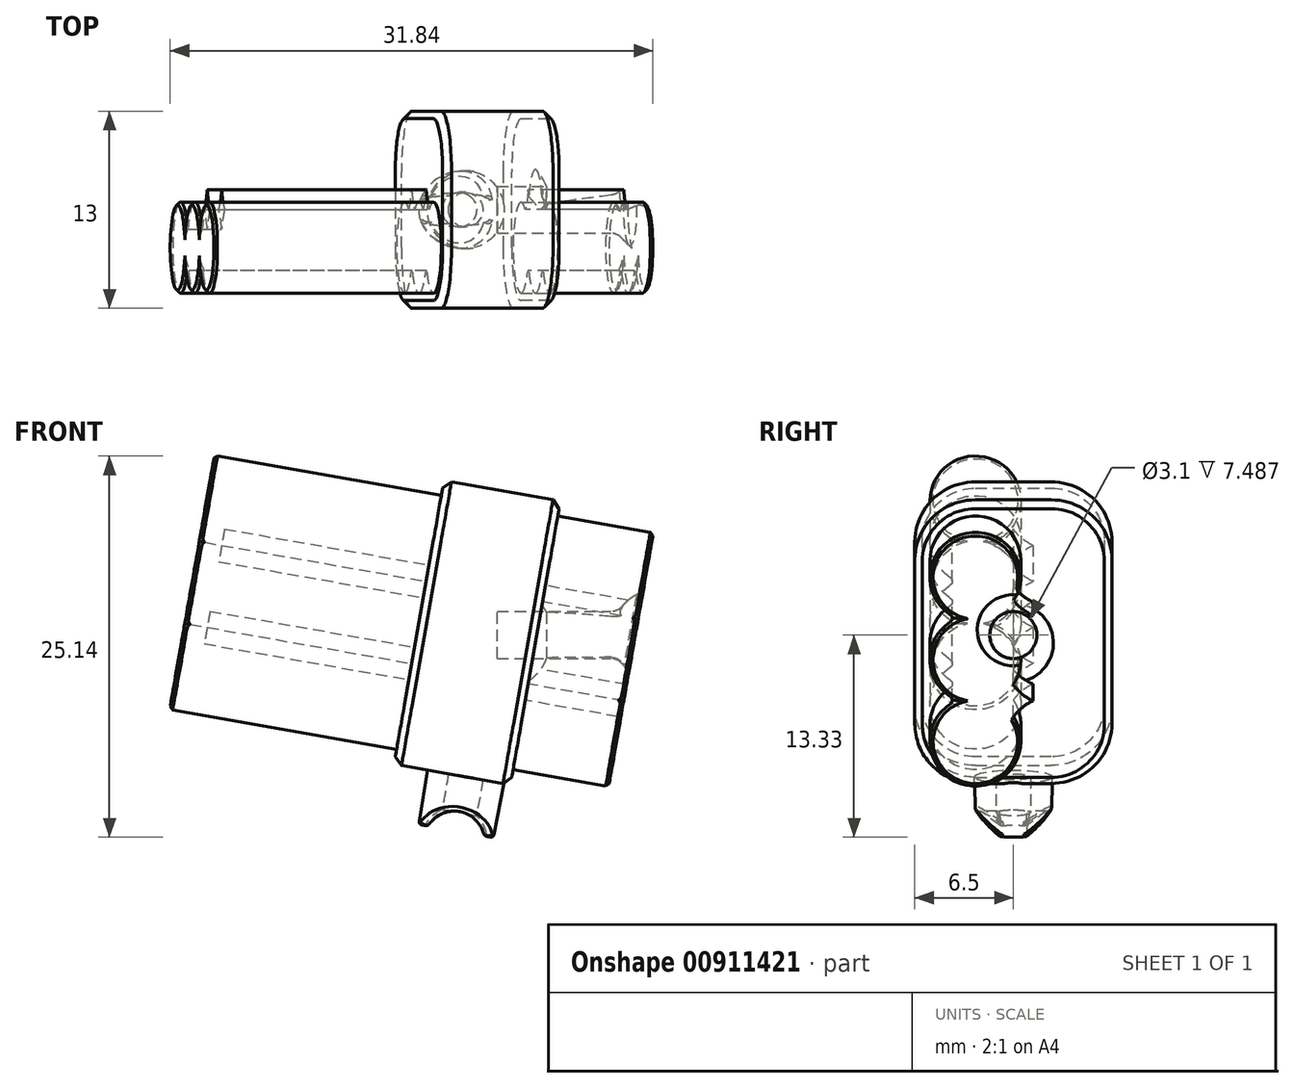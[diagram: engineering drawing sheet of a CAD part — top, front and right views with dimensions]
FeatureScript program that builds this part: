
annotation { "Feature Type Name" : "Feature", "Feature Type Description" : "" }
export const myFeature = defineFeature(function(context is Context, id is Id, definition is map)
    precondition{}
    {
        {
            var Q0;
            Q0=qCreatedBy(makeId("Front.planeOp"),FACE);
            var sketch = newSketch(context, id + "F0", { "sketchPlane" : qUnion([Q0])});
            skCircle(sketch, "E0", {"center": v(0, 0) * mm, "radius": 4 * mm});
            skCircle(sketch, "E1", {"center": v(11, 0) * mm, "radius": 3 * mm, "construction": true});
            skLineSegment(sketch, "E2.bottom", {"start": v(1.43, 1.55) * mm, "end": v(20.57, 1.55) * mm, "construction": true});
            skLineSegment(sketch, "E2.top", {"start": v(1.43, -1.55) * mm, "end": v(20.57, -1.55) * mm, "construction": true});
            skLineSegment(sketch, "E2.left", {"start": v(1.43, 1.55) * mm, "end": v(1.43, -1.55) * mm, "construction": true});
            skLineSegment(sketch, "E2.right", {"start": v(20.57, 1.55) * mm, "end": v(20.57, -1.55) * mm, "construction": true});
            skPoint(sketch, "E3", {"position": v(8.43, 1.55) * mm});
            skLineSegment(sketch, "E4", {"start": v(0, 0) * mm, "end": v(11, 0) * mm, "construction": true});
            skLineSegment(sketch, "E5", {"start": v(0, 0) * mm, "end": v(-2.38, -13.51) * mm, "construction": true});
            skCircle(sketch, "E6", {"center": v(-2.38, -13.51) * mm, "radius": 2 * mm, "construction": true});
            skLineSegment(sketch, "E7", {"start": v(-3.07, -11.63) * mm, "end": v(-2.2, -6.71) * mm, "construction": true});
            skLineSegment(sketch, "E8", {"start": v(-2.2, -6.71) * mm, "end": v(-0.23, -7.06) * mm, "construction": true});
            skLineSegment(sketch, "E9", {"start": v(-0.23, -7.06) * mm, "end": v(-1.1, -11.98) * mm, "construction": true});
            skPoint(sketch, "E10", {"position": v(-1.21, -6.88) * mm});
            skLineSegment(sketch, "E11", {"start": v(-3, -2.64) * mm, "end": v(-4.74, -12.49) * mm});
            skLineSegment(sketch, "E12", {"start": v(-4.74, -12.49) * mm, "end": v(0.18, -13.36) * mm});
            skLineSegment(sketch, "E13", {"start": v(0.18, -13.36) * mm, "end": v(1.92, -3.5) * mm});
            skLineSegment(sketch, "E14", {"start": v(1.92, -3.5) * mm, "end": v(-3, -2.64) * mm, "construction": true});
            skPoint(sketch, "E15", {"position": v(-0.54, -3.08) * mm});
            skSolve(sketch);
        }
        {
            var Q0;
            Q0=qCreatedBy(makeId("Front.planeOp"),FACE);
            var sketch = newSketch(context, id + "F1", { "sketchPlane" : qUnion([Q0])});
            skArc(sketch, "E16.0", {"start": v(0.7, 3.94) * mm, "mid": v(-3.49, 1.96) * mm, "end": v(-3, -2.64) * mm});
            skLineSegment(sketch, "E17.0", {"start": v(-3, -2.64) * mm, "end": v(-4.74, -12.49) * mm});
            skLineSegment(sketch, "E18.0", {"start": v(-4.74, -12.49) * mm, "end": v(-2.28, -12.92) * mm});
            skLineSegment(sketch, "E19.0", {"start": v(0, 0) * mm, "end": v(-2.28, -12.92) * mm});
            skLineSegment(sketch, "E20", {"start": v(0, 0) * mm, "end": v(0.7, 3.94) * mm});
            skPoint(sketch, "E21.orphan", {"position": v(0.18, -13.36) * mm});
            skPoint(sketch, "E22.orphan", {"position": v(-2.38, -13.51) * mm});
            skSolve(sketch);
        }
        {
            var Q0;
            Q0 = qSketchRegion(id + "F1", true);
            var Q1;
            Q1=sQuery(id+"F1.wireOp",EDGE,"E19.0");
            revolve(context, id + "F2", {"surfaceOperationType" : NewSurfaceOperationType.NEW, "entities" : qUnion([Q0]), "axis" : qUnion([Q1]), "revolveType" : RevolveType.FULL});
        }
        {
            var Q0;
            Q0=qCreatedBy(makeId("Front.planeOp"),FACE);
            var sketch = newSketch(context, id + "F3", { "sketchPlane" : qUnion([Q0])});
            skLineSegment(sketch, "E23.0", {"start": v(-2.2, -6.71) * mm, "end": v(-1.21, -6.88) * mm, "construction": true});
            skLineSegment(sketch, "E24.0", {"start": v(-3.07, -11.63) * mm, "end": v(-2.2, -6.71) * mm});
            skArc(sketch, "E25.0", {"start": v(-3.07, -11.63) * mm, "mid": v(-4.38, -13.69) * mm, "end": v(-2.73, -15.48) * mm, "construction": true});
            skLineSegment(sketch, "E26.0", {"start": v(-1.21, -6.88) * mm, "end": v(-2.38, -13.51) * mm});
            skLineSegment(sketch, "E27", {"start": v(-2.38, -13.51) * mm, "end": v(-2.73, -15.48) * mm});
            skPoint(sketch, "E28.orphan", {"position": v(-0.23, -7.06) * mm});
            skPoint(sketch, "E29.orphan", {"position": v(0, 0) * mm});
            skLineSegment(sketch, "E30.0", {"start": v(-3.2, -11.53) * mm, "end": v(-2.17, -5.7) * mm});
            skArc(sketch, "E31.0", {"start": v(-3.2, -11.53) * mm, "mid": v(-4.52, -13.75) * mm, "end": v(-2.76, -15.63) * mm});
            skLineSegment(sketch, "E32.0", {"start": v(-2.17, -5.7) * mm, "end": v(-1.04, -5.9) * mm});
            skLineSegment(sketch, "E33", {"start": v(-2.76, -15.63) * mm, "end": v(-2.73, -15.48) * mm});
            skLineSegment(sketch, "E34", {"start": v(-1.04, -5.9) * mm, "end": v(-1.21, -6.88) * mm});
            skSolve(sketch);
        }
        {
            var Q0;
            Q0 = qSketchRegion(id + "F3", true);
            var Q1;
            Q1=sQuery(id+"F3.wireOp",EDGE,"E27");
            revolve(context, id + "F4", {"operationType" : NewBodyOperationType.REMOVE, "surfaceOperationType" : NewSurfaceOperationType.NEW, "entities" : qUnion([Q0]), "axis" : qUnion([Q1]), "revolveType" : RevolveType.FULL, "oppositeDirection" : true});
        }
        {
            var Q0;
            Q0=qCreatedBy(makeId("Front.planeOp"),FACE);
            var sketch = newSketch(context, id + "F5", { "sketchPlane" : qUnion([Q0])});
            skCircle(sketch, "E35.0", {"center": v(-2.38, -13.51) * mm, "radius": 2 * mm, "construction": true});
            skLineSegment(sketch, "E36.0", {"start": v(0, 0) * mm, "end": v(-2.38, -13.51) * mm, "construction": true});
            skLineSegment(sketch, "E37", {"start": v(-2.38, -13.51) * mm, "end": v(-2.4, -13.61) * mm, "construction": true});
            skCircle(sketch, "E38", {"center": v(-2.4, -13.61) * mm, "radius": 2 * mm});
            skSolve(sketch);
        }
        {
            var Q0;
            Q0=qCreatedBy(makeId("Front.planeOp"),FACE);
            var sketch = newSketch(context, id + "F6", { "sketchPlane" : qUnion([Q0])});
            skLineSegment(sketch, "E39", {"start": v(1.92, -3.5) * mm, "end": v(0.18, -13.36) * mm, "construction": true});
            skLineSegment(sketch, "E40", {"start": v(-4.74, -12.49) * mm, "end": v(-3, -2.64) * mm});
            skLineSegment(sketch, "E41.0", {"start": v(0, 0) * mm, "end": v(-2.38, -13.51) * mm, "construction": true});
            skLineSegment(sketch, "E42", {"start": v(-4.74, -12.49) * mm, "end": v(-3, -1.47) * mm});
            skLineSegment(sketch, "E43", {"start": v(-3, -1.47) * mm, "end": v(-3, -2.64) * mm});
            skSolve(sketch);
        }
        {
            var Q0;
            Q0 = qSketchRegion(id + "F6", true);
            var Q1;
            Q1=sQuery(id+"F6.wireOp",EDGE,"E41.0");
            revolve(context, id + "F7", {"operationType" : NewBodyOperationType.ADD, "surfaceOperationType" : NewSurfaceOperationType.NEW, "entities" : qUnion([Q0]), "axis" : qUnion([Q1]), "revolveType" : RevolveType.FULL});
        }
        {
            var Q0;
            Q0 = qSketchRegion(id + "F5", true);
            extrude(context, id + "F8", {"entities" : qUnion([Q0]), "operationType" : NewBodyOperationType.REMOVE, "endBound" : BoundingType.SYMMETRIC, "oppositeDirection" : true, "depth" : 7.52 * mm, "offsetDistance" : 25 * mm});
        }
        {
            var Q0;
            Q0=qCreatedBy(makeId("Front.planeOp"),FACE);
            cPlane(context, id + "F9", {"entities" : qUnion([Q0]), "cplaneType" : CPlaneType.OFFSET, "offset" : 2.5 * mm, "width" : 150 * mm, "height" : 150 * mm});
        }
        {
            var Q0;
            Q0=qCreatedBy(makeId("Front.planeOp"),FACE);
            var sketch = newSketch(context, id + "F10", { "sketchPlane" : qUnion([Q0])});
            skLineSegment(sketch, "E44", {"start": v(0, 0) * mm, "end": v(4.68, 26.57) * mm});
            skLineSegment(sketch, "E45", {"start": v(4.68, 26.57) * mm, "end": v(4.68, 0) * mm, "construction": true});
            skLineSegment(sketch, "E46", {"start": v(4.68, 0) * mm, "end": v(0, 0) * mm, "construction": true});
            skSolve(sketch);
        }
        {
            var Q0;
            Q0=qCreatedBy(id+"F9.planeOp",FACE);
            var Q1;
            Q1=sQuery(id+"F10.wireOp",EDGE,"E44");
            cPlane(context, id + "F11", {"entities" : qUnion([Q0, Q1]), "cplaneType" : CPlaneType.LINE_ANGLE, "offset" : 25 * mm, "angle" : 90 * degree, "width" : 150 * mm, "height" : 150 * mm});
        }
        {
            var Q0;
            Q0=qCreatedBy(id+"F9.planeOp",FACE);
            var sketch = newSketch(context, id + "F12", { "sketchPlane" : qUnion([Q0])});
            skLineSegment(sketch, "E47.0", {"start": v(0, 0) * mm, "end": v(4.68, 26.57) * mm});
            skArc(sketch, "E48", {"start": v(2.12, -3.4) * mm, "mid": v(0.7, 3.94) * mm, "end": v(-3.15, -2.46) * mm});
            skLineSegment(sketch, "E49", {"start": v(2.12, -3.4) * mm, "end": v(0.18, -13.36) * mm});
            skLineSegment(sketch, "E50", {"start": v(-4.74, -12.49) * mm, "end": v(-3.15, -2.46) * mm});
            skSolve(sketch);
        }
        {
            var Q0;
            Q0=qCreatedBy(id+"F11.planeOp",FACE);
            var sketch = newSketch(context, id + "F13", { "sketchPlane" : qUnion([Q0])});
            skPoint(sketch, "E51.0", {"position": v(2.5, 0) * mm});
            skLineSegment(sketch, "E52.0", {"start": v(2.5, 0) * mm, "end": v(2.5, 26.98) * mm, "construction": true});
            skLineSegment(sketch, "E53", {"start": v(2.5, 0) * mm, "end": v(15.85, 0) * mm, "construction": true});
            skCircle(sketch, "E54", {"center": v(2.5, 0) * mm, "radius": 3 * mm});
            skCircle(sketch, "E55", {"center": v(2.5, 5.5) * mm, "radius": 3 * mm});
            skCircle(sketch, "E56.MirrorC", {"center": v(2.5, -5.5) * mm, "radius": 3 * mm});
            skSolve(sketch);
        }
        {
            var Q0;
            Q0 = qSketchRegion(id + "F13", true);
            extrude(context, id + "F14", {"entities" : qUnion([Q0]), "operationType" : NewBodyOperationType.ADD, "depth" : 20 * mm, "offsetDistance" : 25 * mm, "hasSecondDirection" : true, "secondDirectionOppositeDirection" : true, "secondDirectionDepth" : 9.4 * mm});
        }
        {
            var Q0;
            Q0=qCreatedBy(id+"F11.planeOp",FACE);
            var sketch = newSketch(context, id + "F15", { "sketchPlane" : qUnion([Q0])});
            skArc(sketch, "E57.0.0", {"start": v(3.7, 2.75) * mm, "mid": v(2.5, 8.5) * mm, "end": v(1.3, 2.75) * mm, "construction": true});
            skArc(sketch, "E57.0.1", {"start": v(1.3, 2.75) * mm, "mid": v(-0.5, 0) * mm, "end": v(1.3, -2.75) * mm});
            skArc(sketch, "E57.0.2", {"start": v(1.3, -2.75) * mm, "mid": v(2.5, -8.5) * mm, "end": v(3.7, -2.75) * mm});
            skArc(sketch, "E57.0.3", {"start": v(3.7, -2.75) * mm, "mid": v(5.5, 0) * mm, "end": v(3.7, 2.75) * mm});
            skLineSegment(sketch, "E58.bottom", {"start": v(2.5, -9.5) * mm, "end": v(-2.5, -9.5) * mm});
            skLineSegment(sketch, "E58.top", {"start": v(2.5, 9.5) * mm, "end": v(-2.5, 9.5) * mm});
            skLineSegment(sketch, "E58.left", {"start": v(6.5, -5.5) * mm, "end": v(6.5, 5.5) * mm});
            skLineSegment(sketch, "E58.right", {"start": v(-6.5, -5.5) * mm, "end": v(-6.5, 5.5) * mm});
            skPoint(sketch, "E58.middle", {"position": v(0, 0) * mm});
            skPoint(sketch, "E59.visualSharp", {"position": v(6.5, 9.5) * mm});
            skArc(sketch, "E59.filletArc", {"start": v(6.5, 5.5) * mm, "mid": v(5.33, 8.33) * mm, "end": v(2.5, 9.5) * mm});
            skPoint(sketch, "E60.visualSharp", {"position": v(6.5, -9.5) * mm});
            skArc(sketch, "E60.filletArc", {"start": v(2.5, -9.5) * mm, "mid": v(5.33, -8.33) * mm, "end": v(6.5, -5.5) * mm});
            skPoint(sketch, "E61.visualSharp", {"position": v(-6.5, 9.5) * mm});
            skArc(sketch, "E61.filletArc", {"start": v(-2.5, 9.5) * mm, "mid": v(-5.33, 8.33) * mm, "end": v(-6.5, 5.5) * mm});
            skPoint(sketch, "E62.visualSharp", {"position": v(-6.5, -9.5) * mm});
            skArc(sketch, "E62.filletArc", {"start": v(-6.5, -5.5) * mm, "mid": v(-5.33, -8.33) * mm, "end": v(-2.5, -9.5) * mm});
            skSolve(sketch);
        }
        {
            var Q0;
            Q0 = qSketchRegion(id + "F15", true);
            extrude(context, id + "F16", {"entities" : qUnion([Q0]), "operationType" : NewBodyOperationType.ADD, "depth" : 4.8 * mm, "offsetDistance" : 25 * mm, "hasSecondDirection" : true, "secondDirectionOppositeDirection" : true, "secondDirectionDepth" : 3 * mm});
        }
        {
            var Q0;
            {var subQ0=sQuery(id+"F15.wireOp",EDGE,"E58.right");var subQ1=sQuery(id+"F15.wireOp",EDGE,"E58.left");var subQ2=sQuery(id+"F15.wireOp",EDGE,"E58.bottom");var subQ3=sQuery(id+"F13.wireOp",EDGE,"E56.MirrorC");var subQ4=sQuery(id+"F13.wireOp",EDGE,"E55");var subQ5=sQuery(id+"F15.wireOp",EDGE,"E62.filletArc");var subQ6=sQuery(id+"F13.wireOp",EDGE,"E54");var subQ7=makeQuery(id+"F13.imprint","IMPRINT",EDGE,{"disambiguationData":[TD([[makeQuery(id+"F13.imprint","INTERSECT",VERTEX,{"disambiguationData":[OD(1.0)],"derivedFrom":[subQ6,subQ4]}),1.0]])],"derivedFrom":subQ6});var subQ8=sQuery(id+"F15.wireOp",EDGE,"E58.top");var subQ9=sQuery(id+"F15.wireOp",EDGE,"E61.filletArc");var subQ10=sQuery(id+"F15.wireOp",EDGE,"E59.filletArc");var subQ11=sQuery(id+"F15.wireOp",EDGE,"E60.filletArc");Q0=makeQuery(id+"F16.boolean.opBoolean","SPLIT",FACE,{"disambiguationData":[TD([makeQuery(id+"F14.opExtrude","SWEPT_FACE",FACE,{"disambiguationData":[OSD([subQ6]),TDD([subQ7])]}),makeQuery(id+"F14.opExtrude","SWEPT_FACE",FACE,{"disambiguationData":[OSD([subQ4])]}),makeQuery(id+"F14.opExtrude","SWEPT_FACE",FACE,{"disambiguationData":[OSD([subQ3])]}),makeQuery(id+"FyxM6r6C1p8SssR_1.1.F14.opExtrude","SWEPT_FACE",FACE,{"disambiguationData":[OSD([subQ6]),TDD([subQ7])]}),makeQuery(id+"FyxM6r6C1p8SssR_1.1.F14.opExtrude","SWEPT_FACE",FACE,{"disambiguationData":[OSD([subQ4])]}),makeQuery(id+"FyxM6r6C1p8SssR_1.1.F14.opExtrude","SWEPT_FACE",FACE,{"disambiguationData":[OSD([subQ3])]}),makeQuery(id+"F16.opExtrude","SWEPT_FACE",FACE,{"disambiguationData":[OSD([subQ2])]}),makeQuery(id+"F16.opExtrude","SWEPT_FACE",FACE,{"disambiguationData":[OSD([subQ8])]}),makeQuery(id+"F16.opExtrude","SWEPT_FACE",FACE,{"disambiguationData":[OSD([subQ1])]}),makeQuery(id+"F16.opExtrude","SWEPT_FACE",FACE,{"disambiguationData":[OSD([subQ0])]}),makeQuery(id+"F16.opExtrude","SWEPT_FACE",FACE,{"disambiguationData":[OSD([subQ10])]}),makeQuery(id+"F16.opExtrude","SWEPT_FACE",FACE,{"disambiguationData":[OSD([subQ11])]}),makeQuery(id+"F16.opExtrude","SWEPT_FACE",FACE,{"disambiguationData":[OSD([subQ9])]}),makeQuery(id+"F16.opExtrude","SWEPT_FACE",FACE,{"disambiguationData":[OSD([subQ5])]})])],"derivedFrom":makeQuery(id+"F16.opExtrude","CAP_FACE",FACE,{"disambiguationData":[OSD([subQ2,subQ8,subQ1,subQ0,subQ10,subQ11,subQ9,subQ5])],"isStart":false})});}
            var sketch = newSketch(context, id + "F17", { "sketchPlane" : qUnion([Q0])});
            skArc(sketch, "E63.0", {"start": v(0, 3.84) * mm, "mid": v(-0.57, 3.2) * mm, "end": v(-1.3, 2.75) * mm});
            skArc(sketch, "E64.0", {"start": v(0, 3.84) * mm, "mid": v(0.57, 3.2) * mm, "end": v(1.3, 2.75) * mm});
            skArc(sketch, "E65.0", {"start": v(-1.3, 2.75) * mm, "mid": v(-0.57, 2.3) * mm, "end": v(0, 1.66) * mm});
            skArc(sketch, "E66.0", {"start": v(1.3, 2.75) * mm, "mid": v(0.57, 2.3) * mm, "end": v(0, 1.66) * mm});
            skArc(sketch, "E67.0", {"start": v(0, -1.66) * mm, "mid": v(-0.57, -2.3) * mm, "end": v(-1.3, -2.75) * mm});
            skArc(sketch, "E68.0", {"start": v(0, -1.66) * mm, "mid": v(0.57, -2.3) * mm, "end": v(1.3, -2.75) * mm});
            skArc(sketch, "E69.0", {"start": v(0, -3.84) * mm, "mid": v(0.57, -3.2) * mm, "end": v(1.3, -2.75) * mm});
            skArc(sketch, "E70.0", {"start": v(0, -3.84) * mm, "mid": v(-0.57, -3.2) * mm, "end": v(-1.3, -2.75) * mm});
            skSolve(sketch);
        }
        {
            var Q0;
            Q0 = qSketchRegion(id + "F17", true);
            var Q1;
            {var subQ0=sQuery(id+"F13.wireOp",EDGE,"E56.MirrorC");var subQ1=sQuery(id+"F13.wireOp",EDGE,"E55");var subQ2=sQuery(id+"F13.wireOp",EDGE,"E54");Q1=makeQuery(id+"FyxM6r6C1p8SssR_1.1.F14.boolean.opBoolean","MERGE",FACE,{"derivedFrom":[makeQuery(id+"F14.opExtrude","CAP_FACE",FACE,{"disambiguationData":[OSD([subQ2,subQ1,subQ0])],"isStart":false}),makeQuery(id+"FyxM6r6C1p8SssR_1.1.F14.opExtrude","CAP_FACE",FACE,{"disambiguationData":[OSD([subQ2,subQ1,subQ0])],"isStart":false})]});}
            var Q2;
            {var subQ0=sQuery(id+"F13.wireOp",EDGE,"E55");Q2=makeQuery(id+"FyxM6r6C1p8SssR_1.1.F14.boolean.opBoolean","INTERSECT",VERTEX,{"disambiguationData":[OD(2.0)],"derivedFrom":[makeQuery(id+"F14.opExtrude","SWEPT_FACE",FACE,{"disambiguationData":[OSD([subQ0])]}),makeQuery(id+"FyxM6r6C1p8SssR_1.1.F14.opExtrude","SWEPT_FACE",FACE,{"disambiguationData":[OSD([subQ0])]})]});}
            extrude(context, id + "F18", {"entities" : qUnion([Q0]), "operationType" : NewBodyOperationType.ADD, "endBound" : BoundingType.UP_TO_SURFACE, "depth" : 25 * mm, "endBoundEntityFace" : qUnion([Q1]), "endBoundEntityVertex" : qUnion([Q2]), "hasOffset" : true, "offsetDistance" : 1.5 * mm});
        }
        {
            var Q0;
            {var subQ0=sQuery(id+"F15.wireOp",EDGE,"E58.right");var subQ1=sQuery(id+"F15.wireOp",EDGE,"E58.left");var subQ2=sQuery(id+"F15.wireOp",EDGE,"E58.bottom");var subQ3=sQuery(id+"F13.wireOp",EDGE,"E56.MirrorC");var subQ4=sQuery(id+"F13.wireOp",EDGE,"E55");var subQ5=sQuery(id+"F15.wireOp",EDGE,"E62.filletArc");var subQ6=sQuery(id+"F13.wireOp",EDGE,"E54");var subQ7=makeQuery(id+"F13.imprint","IMPRINT",EDGE,{"disambiguationData":[TD([[makeQuery(id+"F13.imprint","INTERSECT",VERTEX,{"disambiguationData":[OD(1.0)],"derivedFrom":[subQ6,subQ4]}),1.0]])],"derivedFrom":subQ6});var subQ8=sQuery(id+"F15.wireOp",EDGE,"E58.top");var subQ9=sQuery(id+"F15.wireOp",EDGE,"E61.filletArc");var subQ10=sQuery(id+"F15.wireOp",EDGE,"E59.filletArc");var subQ11=sQuery(id+"F15.wireOp",EDGE,"E60.filletArc");Q0=makeQuery(id+"F16.boolean.opBoolean","SPLIT",FACE,{"disambiguationData":[TD([makeQuery(id+"F14.opExtrude","SWEPT_FACE",FACE,{"disambiguationData":[OSD([subQ6]),TDD([subQ7])]}),makeQuery(id+"F14.opExtrude","SWEPT_FACE",FACE,{"disambiguationData":[OSD([subQ4])]}),makeQuery(id+"F14.opExtrude","SWEPT_FACE",FACE,{"disambiguationData":[OSD([subQ3])]}),makeQuery(id+"FyxM6r6C1p8SssR_1.1.F14.opExtrude","SWEPT_FACE",FACE,{"disambiguationData":[OSD([subQ6]),TDD([subQ7])]}),makeQuery(id+"FyxM6r6C1p8SssR_1.1.F14.opExtrude","SWEPT_FACE",FACE,{"disambiguationData":[OSD([subQ4])]}),makeQuery(id+"FyxM6r6C1p8SssR_1.1.F14.opExtrude","SWEPT_FACE",FACE,{"disambiguationData":[OSD([subQ3])]}),makeQuery(id+"F16.opExtrude","SWEPT_FACE",FACE,{"disambiguationData":[OSD([subQ2])]}),makeQuery(id+"F16.opExtrude","SWEPT_FACE",FACE,{"disambiguationData":[OSD([subQ8])]}),makeQuery(id+"F16.opExtrude","SWEPT_FACE",FACE,{"disambiguationData":[OSD([subQ1])]}),makeQuery(id+"F16.opExtrude","SWEPT_FACE",FACE,{"disambiguationData":[OSD([subQ0])]}),makeQuery(id+"F16.opExtrude","SWEPT_FACE",FACE,{"disambiguationData":[OSD([subQ10])]}),makeQuery(id+"F16.opExtrude","SWEPT_FACE",FACE,{"disambiguationData":[OSD([subQ11])]}),makeQuery(id+"F16.opExtrude","SWEPT_FACE",FACE,{"disambiguationData":[OSD([subQ9])]}),makeQuery(id+"F16.opExtrude","SWEPT_FACE",FACE,{"disambiguationData":[OSD([subQ5])]})])],"derivedFrom":makeQuery(id+"F16.opExtrude","CAP_FACE",FACE,{"disambiguationData":[OSD([subQ2,subQ8,subQ1,subQ0,subQ10,subQ11,subQ9,subQ5])],"isStart":true})});}
            var sketch = newSketch(context, id + "F19", { "sketchPlane" : qUnion([Q0])});
            skArc(sketch, "E71.0", {"start": v(0, 3.84) * mm, "mid": v(0.57, 3.2) * mm, "end": v(1.3, 2.75) * mm});
            skArc(sketch, "E71.1", {"start": v(0, 3.84) * mm, "mid": v(-0.57, 3.2) * mm, "end": v(-1.3, 2.75) * mm});
            skArc(sketch, "E71.2", {"start": v(1.3, 2.75) * mm, "mid": v(0.57, 2.3) * mm, "end": v(0, 1.66) * mm});
            skArc(sketch, "E71.3", {"start": v(-1.3, 2.75) * mm, "mid": v(-0.57, 2.3) * mm, "end": v(0, 1.66) * mm});
            skArc(sketch, "E71.4", {"start": v(0, -1.66) * mm, "mid": v(0.57, -2.3) * mm, "end": v(1.3, -2.75) * mm});
            skArc(sketch, "E71.5", {"start": v(0, -1.66) * mm, "mid": v(-0.57, -2.3) * mm, "end": v(-1.3, -2.75) * mm});
            skArc(sketch, "E71.6", {"start": v(0, -3.84) * mm, "mid": v(-0.57, -3.2) * mm, "end": v(-1.3, -2.75) * mm});
            skArc(sketch, "E71.7", {"start": v(0, -3.84) * mm, "mid": v(0.57, -3.2) * mm, "end": v(1.3, -2.75) * mm});
            skSolve(sketch);
        }
        {
            var Q0;
            Q0 = qSketchRegion(id + "F19", true);
            var Q1;
            {var subQ0=sQuery(id+"F13.wireOp",EDGE,"E56.MirrorC");var subQ1=sQuery(id+"F13.wireOp",EDGE,"E55");var subQ2=sQuery(id+"F13.wireOp",EDGE,"E54");Q1=makeQuery(id+"FyxM6r6C1p8SssR_1.1.F14.boolean.opBoolean","MERGE",FACE,{"derivedFrom":[makeQuery(id+"F14.opExtrude","CAP_FACE",FACE,{"disambiguationData":[OSD([subQ2,subQ1,subQ0])],"isStart":true}),makeQuery(id+"FyxM6r6C1p8SssR_1.1.F14.opExtrude","CAP_FACE",FACE,{"disambiguationData":[OSD([subQ2,subQ1,subQ0])],"isStart":true})]});}
            extrude(context, id + "F20", {"entities" : qUnion([Q0]), "operationType" : NewBodyOperationType.ADD, "endBound" : BoundingType.UP_TO_SURFACE, "depth" : 25 * mm, "endBoundEntityFace" : qUnion([Q1]), "offsetDistance" : 1.5 * mm});
        }
        {
            var Q0;
            Q0=makeQuery(id+"F16.opExtrude","CAP_EDGE",EDGE,{"disambiguationData":[OSD([sQuery(id+"F15.wireOp",EDGE,"E58.left")])],"isStart":false});
            var Q1;
            Q1=makeQuery(id+"F16.opExtrude","CAP_EDGE",EDGE,{"disambiguationData":[OSD([sQuery(id+"F15.wireOp",EDGE,"E59.filletArc")])],"isStart":true});
            chamfer(context, id + "F21", {"entities" : qUnion([Q0, Q1]), "width" : 0.5 * mm, "tangentPropagation" : true});
        }
        {
            var Q0;
            Q0=qCreatedBy(makeId("Front.planeOp"),FACE);
            var sketch = newSketch(context, id + "F22", { "sketchPlane" : qUnion([Q0])});
            skLineSegment(sketch, "E72.0", {"start": v(8.15, -1.55) * mm, "end": v(8.27, -1.55) * mm});
            skLineSegment(sketch, "E73.0", {"start": v(1.43, 0) * mm, "end": v(1.43, -1.55) * mm});
            skPoint(sketch, "E74.0", {"position": v(20.57, 0) * mm});
            skLineSegment(sketch, "E75.0", {"start": v(20.57, 1.55) * mm, "end": v(20.57, -1.55) * mm});
            skLineSegment(sketch, "E76.0", {"start": v(0.43, 1.55) * mm, "end": v(8.43, 1.55) * mm});
            skLineSegment(sketch, "E77.0", {"start": v(0.43, 1.55) * mm, "end": v(0.43, 0) * mm});
            skLineSegment(sketch, "E78", {"start": v(20.57, 1.55) * mm, "end": v(20.57, 0) * mm});
            skLineSegment(sketch, "E79", {"start": v(0.43, 0) * mm, "end": v(20.57, 0) * mm});
            skArc(sketch, "E80.trimOffspring", {"start": v(13.57, 1.55) * mm, "mid": v(11, 3) * mm, "end": v(8.43, 1.55) * mm});
            skLineSegment(sketch, "E81.trimOffspring", {"start": v(13.57, 1.55) * mm, "end": v(20.57, 1.55) * mm});
            skPoint(sketch, "E82.orphan", {"position": v(1.43, 1.55) * mm});
            skPoint(sketch, "E83.orphan", {"position": v(20.57, -1.55) * mm});
            skPoint(sketch, "E84.orphan", {"position": v(1.43, -1.55) * mm});
            skLineSegment(sketch, "E85.trimOffspring", {"start": v(11.73, -1.55) * mm, "end": v(11.85, -1.55) * mm});
            skPoint(sketch, "E86.0.end.orphan", {"position": v(20.57, 1.55) * mm});
            skSolve(sketch);
        }
        {
            var Q0;
            Q0=makeQuery(id+"F22.imprint","IMPRINT",FACE,{"disambiguationData":[TD([[makeQuery(id+"F22.imprint","IMPRINT",EDGE,{"derivedFrom":sQuery(id+"F22.wireOp",EDGE,"E76.0")}),-1.0]])]});
            var Q1;
            Q1=sQuery(id+"F22.wireOp",EDGE,"E79");
            revolve(context, id + "F23", {"operationType" : NewBodyOperationType.REMOVE, "surfaceOperationType" : NewSurfaceOperationType.NEW, "entities" : qUnion([Q0]), "axis" : qUnion([Q1]), "revolveType" : RevolveType.FULL, "oppositeDirection" : true});
        }
        {
            var Q0;
            {var subQ1=sQuery(id+"F13.wireOp",EDGE,"E55");var subQ2=sQuery(id+"F13.wireOp",EDGE,"E54");Q0=makeQuery(id+"FyxM6r6C1p8SssR_1.1.F14.boolean.opBoolean","SPLIT",EDGE,{"disambiguationData":[TD([makeQuery(id+"F14.opExtrude","SWEPT_FACE",FACE,{"disambiguationData":[OSD([subQ2]),TDD([makeQuery(id+"F13.imprint","IMPRINT",EDGE,{"disambiguationData":[TD([[makeQuery(id+"F13.imprint","INTERSECT",VERTEX,{"disambiguationData":[OD(1.0)],"derivedFrom":[subQ2,subQ1]}),1.0]])],"derivedFrom":subQ2})])]})])],"derivedFrom":makeQuery(id+"F14.opExtrude","CAP_EDGE",EDGE,{"disambiguationData":[OSD([subQ1])],"isStart":false})});}
            var Q1;
            {var subQ0=sQuery(id+"F13.wireOp",EDGE,"E54");Q1=makeQuery(id+"F14.opExtrude","CAP_EDGE",EDGE,{"disambiguationData":[OSD([subQ0]),TDD([makeQuery(id+"F13.imprint","IMPRINT",EDGE,{"disambiguationData":[TD([[makeQuery(id+"F13.imprint","INTERSECT",VERTEX,{"disambiguationData":[OD(1.0)],"derivedFrom":[subQ0,sQuery(id+"F13.wireOp",EDGE,"E55")]}),1.0]])],"derivedFrom":subQ0})])],"isStart":false});}
            var Q2;
            {var subQ0=sQuery(id+"F13.wireOp",EDGE,"E56.MirrorC");var subQ1=sQuery(id+"F13.wireOp",EDGE,"E55");var subQ2=sQuery(id+"F13.wireOp",EDGE,"E54");Q2=makeQuery(id+"FyxM6r6C1p8SssR_1.1.F14.boolean.opBoolean","SPLIT",EDGE,{"disambiguationData":[TD([makeQuery(id+"F14.opExtrude","SWEPT_FACE",FACE,{"disambiguationData":[OSD([subQ2]),TDD([makeQuery(id+"F13.imprint","IMPRINT",EDGE,{"disambiguationData":[TD([[makeQuery(id+"F13.imprint","INTERSECT",VERTEX,{"disambiguationData":[OD(1.0)],"derivedFrom":[subQ2,subQ1]}),1.0]])],"derivedFrom":subQ2})])]})])],"derivedFrom":makeQuery(id+"F14.opExtrude","CAP_EDGE",EDGE,{"disambiguationData":[OSD([subQ0])],"isStart":false})});}
            var Q3;
            {var subQ0=sQuery(id+"F13.wireOp",EDGE,"E56.MirrorC");var subQ1=sQuery(id+"F13.wireOp",EDGE,"E55");var subQ2=sQuery(id+"F13.wireOp",EDGE,"E54");Q3=makeQuery(id+"FyxM6r6C1p8SssR_1.1.F14.boolean.opBoolean","SPLIT",EDGE,{"disambiguationData":[TD([makeQuery(id+"FyxM6r6C1p8SssR_1.1.F14.opExtrude","SWEPT_FACE",FACE,{"disambiguationData":[OSD([subQ2]),TDD([makeQuery(id+"F13.imprint","IMPRINT",EDGE,{"disambiguationData":[TD([[makeQuery(id+"F13.imprint","INTERSECT",VERTEX,{"disambiguationData":[OD(1.0)],"derivedFrom":[subQ2,subQ1]}),1.0]])],"derivedFrom":subQ2})])]})])],"derivedFrom":makeQuery(id+"FyxM6r6C1p8SssR_1.1.F14.opExtrude","CAP_EDGE",EDGE,{"disambiguationData":[OSD([subQ0])],"isStart":false})});}
            var Q4;
            {var subQ0=sQuery(id+"F13.wireOp",EDGE,"E54");Q4=makeQuery(id+"FyxM6r6C1p8SssR_1.1.F14.opExtrude","CAP_EDGE",EDGE,{"disambiguationData":[OSD([subQ0]),TDD([makeQuery(id+"F13.imprint","IMPRINT",EDGE,{"disambiguationData":[TD([[makeQuery(id+"F13.imprint","INTERSECT",VERTEX,{"disambiguationData":[OD(1.0)],"derivedFrom":[subQ0,sQuery(id+"F13.wireOp",EDGE,"E55")]}),1.0]])],"derivedFrom":subQ0})])],"isStart":false});}
            var Q5;
            {var subQ1=sQuery(id+"F13.wireOp",EDGE,"E55");var subQ2=sQuery(id+"F13.wireOp",EDGE,"E54");Q5=makeQuery(id+"FyxM6r6C1p8SssR_1.1.F14.boolean.opBoolean","SPLIT",EDGE,{"disambiguationData":[TD([makeQuery(id+"FyxM6r6C1p8SssR_1.1.F14.opExtrude","SWEPT_FACE",FACE,{"disambiguationData":[OSD([subQ2]),TDD([makeQuery(id+"F13.imprint","IMPRINT",EDGE,{"disambiguationData":[TD([[makeQuery(id+"F13.imprint","INTERSECT",VERTEX,{"disambiguationData":[OD(1.0)],"derivedFrom":[subQ2,subQ1]}),1.0]])],"derivedFrom":subQ2})])]})])],"derivedFrom":makeQuery(id+"FyxM6r6C1p8SssR_1.1.F14.opExtrude","CAP_EDGE",EDGE,{"disambiguationData":[OSD([subQ1])],"isStart":false})});}
            var Q6;
            {var subQ0=sQuery(id+"F13.wireOp",EDGE,"E56.MirrorC");var subQ1=sQuery(id+"F13.wireOp",EDGE,"E55");var subQ2=sQuery(id+"F13.wireOp",EDGE,"E54");var subQ3=makeQuery(id+"F13.imprint","IMPRINT",EDGE,{"disambiguationData":[TD([[makeQuery(id+"F13.imprint","INTERSECT",VERTEX,{"disambiguationData":[OD(0.0)],"derivedFrom":[subQ2,subQ1]}),-1.0]])],"derivedFrom":subQ2});Q6=makeQuery(id+"FyxM6r6C1p8SssR_1.1.F14.boolean.opBoolean","SPLIT",EDGE,{"disambiguationData":[TD([makeQuery(id+"FyxM6r6C1p8SssR_1.1.F14.opExtrude","SWEPT_FACE",FACE,{"disambiguationData":[OSD([subQ0])]})])],"derivedFrom":makeQuery(id+"FyxM6r6C1p8SssR_1.1.F14.opExtrude","CAP_EDGE",EDGE,{"disambiguationData":[OSD([subQ2]),TDD([subQ3])],"isStart":false})});}
            var Q7;
            {var subQ0=sQuery(id+"F13.wireOp",EDGE,"E56.MirrorC");var subQ1=sQuery(id+"F13.wireOp",EDGE,"E55");var subQ2=sQuery(id+"F13.wireOp",EDGE,"E54");Q7=makeQuery(id+"FyxM6r6C1p8SssR_1.1.F14.boolean.opBoolean","SPLIT",EDGE,{"disambiguationData":[TD([makeQuery(id+"FyxM6r6C1p8SssR_1.1.F14.opExtrude","SWEPT_FACE",FACE,{"disambiguationData":[OSD([subQ2]),TDD([makeQuery(id+"F13.imprint","IMPRINT",EDGE,{"disambiguationData":[TD([[makeQuery(id+"F13.imprint","INTERSECT",VERTEX,{"disambiguationData":[OD(0.0)],"derivedFrom":[subQ2,subQ1]}),-1.0]])],"derivedFrom":subQ2})])]})])],"derivedFrom":makeQuery(id+"FyxM6r6C1p8SssR_1.1.F14.opExtrude","CAP_EDGE",EDGE,{"disambiguationData":[OSD([subQ0])],"isStart":false})});}
            var Q8;
            {var subQ0=sQuery(id+"F13.wireOp",EDGE,"E56.MirrorC");var subQ1=sQuery(id+"F13.wireOp",EDGE,"E55");var subQ2=sQuery(id+"F13.wireOp",EDGE,"E54");Q8=makeQuery(id+"FyxM6r6C1p8SssR_1.1.F14.boolean.opBoolean","SPLIT",EDGE,{"disambiguationData":[TD([makeQuery(id+"F14.opExtrude","SWEPT_FACE",FACE,{"disambiguationData":[OSD([subQ2]),TDD([makeQuery(id+"F13.imprint","IMPRINT",EDGE,{"disambiguationData":[TD([[makeQuery(id+"F13.imprint","INTERSECT",VERTEX,{"disambiguationData":[OD(0.0)],"derivedFrom":[subQ2,subQ1]}),-1.0]])],"derivedFrom":subQ2})])]})])],"derivedFrom":makeQuery(id+"F14.opExtrude","CAP_EDGE",EDGE,{"disambiguationData":[OSD([subQ0])],"isStart":false})});}
            var Q9;
            {var subQ0=sQuery(id+"F13.wireOp",EDGE,"E55");var subQ1=sQuery(id+"F13.wireOp",EDGE,"E54");var subQ2=sQuery(id+"F13.wireOp",EDGE,"E56.MirrorC");var subQ3=makeQuery(id+"F13.imprint","IMPRINT",EDGE,{"disambiguationData":[TD([[makeQuery(id+"F13.imprint","INTERSECT",VERTEX,{"disambiguationData":[OD(0.0)],"derivedFrom":[subQ1,subQ0]}),-1.0]])],"derivedFrom":subQ1});Q9=makeQuery(id+"FyxM6r6C1p8SssR_1.1.F14.boolean.opBoolean","SPLIT",EDGE,{"disambiguationData":[TD([makeQuery(id+"F14.opExtrude","SWEPT_FACE",FACE,{"disambiguationData":[OSD([subQ2])]})])],"derivedFrom":makeQuery(id+"F14.opExtrude","CAP_EDGE",EDGE,{"disambiguationData":[OSD([subQ1]),TDD([subQ3])],"isStart":false})});}
            var Q10;
            {var subQ1=sQuery(id+"F13.wireOp",EDGE,"E55");var subQ2=sQuery(id+"F13.wireOp",EDGE,"E54");var subQ3=makeQuery(id+"F13.imprint","IMPRINT",EDGE,{"disambiguationData":[TD([[makeQuery(id+"F13.imprint","INTERSECT",VERTEX,{"disambiguationData":[OD(0.0)],"derivedFrom":[subQ2,subQ1]}),-1.0]])],"derivedFrom":subQ2});Q10=makeQuery(id+"FyxM6r6C1p8SssR_1.1.F14.boolean.opBoolean","SPLIT",EDGE,{"disambiguationData":[TD([makeQuery(id+"FyxM6r6C1p8SssR_1.1.F14.opExtrude","SWEPT_FACE",FACE,{"disambiguationData":[OSD([subQ1])]})])],"derivedFrom":makeQuery(id+"FyxM6r6C1p8SssR_1.1.F14.opExtrude","CAP_EDGE",EDGE,{"disambiguationData":[OSD([subQ2]),TDD([subQ3])],"isStart":false})});}
            var Q11;
            {var subQ1=sQuery(id+"F13.wireOp",EDGE,"E55");var subQ2=sQuery(id+"F13.wireOp",EDGE,"E54");Q11=makeQuery(id+"FyxM6r6C1p8SssR_1.1.F14.boolean.opBoolean","SPLIT",EDGE,{"disambiguationData":[TD([makeQuery(id+"FyxM6r6C1p8SssR_1.1.F14.opExtrude","SWEPT_FACE",FACE,{"disambiguationData":[OSD([subQ2]),TDD([makeQuery(id+"F13.imprint","IMPRINT",EDGE,{"disambiguationData":[TD([[makeQuery(id+"F13.imprint","INTERSECT",VERTEX,{"disambiguationData":[OD(0.0)],"derivedFrom":[subQ2,subQ1]}),-1.0]])],"derivedFrom":subQ2})])]})])],"derivedFrom":makeQuery(id+"FyxM6r6C1p8SssR_1.1.F14.opExtrude","CAP_EDGE",EDGE,{"disambiguationData":[OSD([subQ1])],"isStart":false})});}
            var Q12;
            {var subQ1=sQuery(id+"F13.wireOp",EDGE,"E55");var subQ2=sQuery(id+"F13.wireOp",EDGE,"E54");Q12=makeQuery(id+"FyxM6r6C1p8SssR_1.1.F14.boolean.opBoolean","SPLIT",EDGE,{"disambiguationData":[TD([makeQuery(id+"F14.opExtrude","SWEPT_FACE",FACE,{"disambiguationData":[OSD([subQ2]),TDD([makeQuery(id+"F13.imprint","IMPRINT",EDGE,{"disambiguationData":[TD([[makeQuery(id+"F13.imprint","INTERSECT",VERTEX,{"disambiguationData":[OD(0.0)],"derivedFrom":[subQ2,subQ1]}),-1.0]])],"derivedFrom":subQ2})])]})])],"derivedFrom":makeQuery(id+"F14.opExtrude","CAP_EDGE",EDGE,{"disambiguationData":[OSD([subQ1])],"isStart":false})});}
            var Q13;
            {var subQ0=sQuery(id+"F13.wireOp",EDGE,"E55");var subQ1=sQuery(id+"F13.wireOp",EDGE,"E54");var subQ3=makeQuery(id+"F13.imprint","IMPRINT",EDGE,{"disambiguationData":[TD([[makeQuery(id+"F13.imprint","INTERSECT",VERTEX,{"disambiguationData":[OD(0.0)],"derivedFrom":[subQ1,subQ0]}),-1.0]])],"derivedFrom":subQ1});Q13=makeQuery(id+"FyxM6r6C1p8SssR_1.1.F14.boolean.opBoolean","SPLIT",EDGE,{"disambiguationData":[TD([makeQuery(id+"F14.opExtrude","SWEPT_FACE",FACE,{"disambiguationData":[OSD([subQ0])]})])],"derivedFrom":makeQuery(id+"F14.opExtrude","CAP_EDGE",EDGE,{"disambiguationData":[OSD([subQ1]),TDD([subQ3])],"isStart":false})});}
            chamfer(context, id + "F24", {"entities" : qUnion([Q0, Q1, Q2, Q3, Q4, Q5, Q6, Q7, Q8, Q9, Q10, Q11, Q12, Q13]), "width" : 0.2 * mm, "tangentPropagation" : true});
        }
        {
            var Q0;
            {var subQ1=sQuery(id+"F13.wireOp",EDGE,"E55");var subQ2=sQuery(id+"F13.wireOp",EDGE,"E54");Q0=makeQuery(id+"FyxM6r6C1p8SssR_1.1.F14.boolean.opBoolean","SPLIT",EDGE,{"disambiguationData":[TD([makeQuery(id+"F14.opExtrude","SWEPT_FACE",FACE,{"disambiguationData":[OSD([subQ2]),TDD([makeQuery(id+"F13.imprint","IMPRINT",EDGE,{"disambiguationData":[TD([[makeQuery(id+"F13.imprint","INTERSECT",VERTEX,{"disambiguationData":[OD(1.0)],"derivedFrom":[subQ2,subQ1]}),1.0]])],"derivedFrom":subQ2})])]})])],"derivedFrom":makeQuery(id+"F14.opExtrude","CAP_EDGE",EDGE,{"disambiguationData":[OSD([subQ1])],"isStart":true})});}
            var Q1;
            {var subQ0=sQuery(id+"F13.wireOp",EDGE,"E55");var subQ1=sQuery(id+"F13.wireOp",EDGE,"E54");Q1=makeQuery(id+"FyxM6r6C1p8SssR_1.1.F14.boolean.opBoolean","SPLIT",EDGE,{"disambiguationData":[TD([makeQuery(id+"FyxM6r6C1p8SssR_1.1.F14.opExtrude","SWEPT_FACE",FACE,{"disambiguationData":[OSD([subQ1]),TDD([makeQuery(id+"F13.imprint","IMPRINT",EDGE,{"disambiguationData":[TD([[makeQuery(id+"F13.imprint","INTERSECT",VERTEX,{"disambiguationData":[OD(1.0)],"derivedFrom":[subQ1,subQ0]}),1.0]])],"derivedFrom":subQ1})])]})])],"derivedFrom":makeQuery(id+"FyxM6r6C1p8SssR_1.1.F14.opExtrude","CAP_EDGE",EDGE,{"disambiguationData":[OSD([subQ0])],"isStart":true})});}
            var Q2;
            {var subQ0=sQuery(id+"F13.wireOp",EDGE,"E54");Q2=makeQuery(id+"FyxM6r6C1p8SssR_1.1.F14.opExtrude","CAP_EDGE",EDGE,{"disambiguationData":[OSD([subQ0]),TDD([makeQuery(id+"F13.imprint","IMPRINT",EDGE,{"disambiguationData":[TD([[makeQuery(id+"F13.imprint","INTERSECT",VERTEX,{"disambiguationData":[OD(1.0)],"derivedFrom":[subQ0,sQuery(id+"F13.wireOp",EDGE,"E55")]}),1.0]])],"derivedFrom":subQ0})])],"isStart":true});}
            var Q3;
            {var subQ0=sQuery(id+"F13.wireOp",EDGE,"E54");Q3=makeQuery(id+"F14.opExtrude","CAP_EDGE",EDGE,{"disambiguationData":[OSD([subQ0]),TDD([makeQuery(id+"F13.imprint","IMPRINT",EDGE,{"disambiguationData":[TD([[makeQuery(id+"F13.imprint","INTERSECT",VERTEX,{"disambiguationData":[OD(1.0)],"derivedFrom":[subQ0,sQuery(id+"F13.wireOp",EDGE,"E55")]}),1.0]])],"derivedFrom":subQ0})])],"isStart":true});}
            var Q4;
            {var subQ0=sQuery(id+"F13.wireOp",EDGE,"E56.MirrorC");var subQ1=sQuery(id+"F13.wireOp",EDGE,"E55");var subQ2=sQuery(id+"F13.wireOp",EDGE,"E54");Q4=makeQuery(id+"FyxM6r6C1p8SssR_1.1.F14.boolean.opBoolean","SPLIT",EDGE,{"disambiguationData":[TD([makeQuery(id+"F14.opExtrude","SWEPT_FACE",FACE,{"disambiguationData":[OSD([subQ2]),TDD([makeQuery(id+"F13.imprint","IMPRINT",EDGE,{"disambiguationData":[TD([[makeQuery(id+"F13.imprint","INTERSECT",VERTEX,{"disambiguationData":[OD(1.0)],"derivedFrom":[subQ2,subQ1]}),1.0]])],"derivedFrom":subQ2})])]})])],"derivedFrom":makeQuery(id+"F14.opExtrude","CAP_EDGE",EDGE,{"disambiguationData":[OSD([subQ0])],"isStart":true})});}
            var Q5;
            {var subQ0=sQuery(id+"F13.wireOp",EDGE,"E55");var subQ1=sQuery(id+"F13.wireOp",EDGE,"E54");var subQ2=sQuery(id+"F13.wireOp",EDGE,"E56.MirrorC");Q5=makeQuery(id+"FyxM6r6C1p8SssR_1.1.F14.boolean.opBoolean","SPLIT",EDGE,{"disambiguationData":[TD([makeQuery(id+"FyxM6r6C1p8SssR_1.1.F14.opExtrude","SWEPT_FACE",FACE,{"disambiguationData":[OSD([subQ1]),TDD([makeQuery(id+"F13.imprint","IMPRINT",EDGE,{"disambiguationData":[TD([[makeQuery(id+"F13.imprint","INTERSECT",VERTEX,{"disambiguationData":[OD(1.0)],"derivedFrom":[subQ1,subQ0]}),1.0]])],"derivedFrom":subQ1})])]})])],"derivedFrom":makeQuery(id+"FyxM6r6C1p8SssR_1.1.F14.opExtrude","CAP_EDGE",EDGE,{"disambiguationData":[OSD([subQ2])],"isStart":true})});}
            chamfer(context, id + "F25", {"entities" : qUnion([Q0, Q1, Q2, Q3, Q4, Q5]), "width" : 0.2 * mm, "tangentPropagation" : true});
        }
        {
            var Q0;
            {var subQ0=sQuery(id+"F13.wireOp",EDGE,"E56.MirrorC");var subQ1=sQuery(id+"F13.wireOp",EDGE,"E55");var subQ2=sQuery(id+"F13.wireOp",EDGE,"E54");var subQ3=makeQuery(id+"F13.imprint","INTERSECT",VERTEX,{"disambiguationData":[OD(1.0)],"derivedFrom":[subQ2,subQ1]});Q0=makeQuery(id+"F16.boolean.opBoolean","SPLIT",EDGE,{"disambiguationData":[TD([makeQuery(id+"F14.opExtrude","CAP_FACE",FACE,{"disambiguationData":[OSD([subQ2,subQ1,subQ0])],"isStart":false})])],"derivedFrom":makeQuery(id+"F14.opExtrude","SWEPT_EDGE",EDGE,{"disambiguationData":[OSD([subQ2,subQ1]),TDD([subQ3])]})});}
            var Q1;
            {var subQ0=sQuery(id+"F13.wireOp",EDGE,"E56.MirrorC");var subQ1=sQuery(id+"F13.wireOp",EDGE,"E55");var subQ2=sQuery(id+"F13.wireOp",EDGE,"E54");var subQ3=makeQuery(id+"F13.imprint","INTERSECT",VERTEX,{"disambiguationData":[OD(1.0)],"derivedFrom":[subQ2,subQ0]});Q1=makeQuery(id+"F16.boolean.opBoolean","SPLIT",EDGE,{"disambiguationData":[TD([makeQuery(id+"F14.opExtrude","CAP_FACE",FACE,{"disambiguationData":[OSD([subQ2,subQ1,subQ0])],"isStart":false})])],"derivedFrom":makeQuery(id+"F14.opExtrude","SWEPT_EDGE",EDGE,{"disambiguationData":[OSD([subQ2,subQ0]),TDD([subQ3])]})});}
            var Q2;
            {var subQ0=sQuery(id+"F13.wireOp",EDGE,"E56.MirrorC");Q2=makeQuery(id+"FyxM6r6C1p8SssR_1.1.F14.boolean.opBoolean","INTERSECT",EDGE,{"disambiguationData":[OD(3.0)],"derivedFrom":[makeQuery(id+"F14.boolean.opBoolean","SPLIT",FACE,{"disambiguationData":[TD([makeQuery(id+"F2.opRevolve","SWEPT_FACE",FACE,{"disambiguationData":[OSD([sQuery(id+"F1.wireOp",EDGE,"E16.0")])]})])],"derivedFrom":makeQuery(id+"F14.opExtrude","SWEPT_FACE",FACE,{"disambiguationData":[OSD([subQ0])]})}),makeQuery(id+"FyxM6r6C1p8SssR_1.1.F14.opExtrude","SWEPT_FACE",FACE,{"disambiguationData":[OSD([subQ0])]})]});}
            var Q3;
            {var subQ0=sQuery(id+"F13.wireOp",EDGE,"E56.MirrorC");var subQ1=sQuery(id+"F13.wireOp",EDGE,"E55");var subQ2=sQuery(id+"F13.wireOp",EDGE,"E54");var subQ3=makeQuery(id+"F13.imprint","INTERSECT",VERTEX,{"disambiguationData":[OD(1.0)],"derivedFrom":[subQ2,subQ0]});Q3=makeQuery(id+"F16.boolean.opBoolean","SPLIT",EDGE,{"disambiguationData":[TD([makeQuery(id+"F14.opExtrude","CAP_FACE",FACE,{"disambiguationData":[OSD([subQ2,subQ1,subQ0])],"isStart":false})])],"derivedFrom":makeQuery(id+"FyxM6r6C1p8SssR_1.1.F14.opExtrude","SWEPT_EDGE",EDGE,{"disambiguationData":[OSD([subQ2,subQ0]),TDD([subQ3])]})});}
            var Q4;
            {var subQ0=sQuery(id+"F13.wireOp",EDGE,"E55");var subQ1=sQuery(id+"F13.wireOp",EDGE,"E56.MirrorC");var subQ2=sQuery(id+"F13.wireOp",EDGE,"E54");var subQ3=makeQuery(id+"F13.imprint","INTERSECT",VERTEX,{"disambiguationData":[OD(1.0)],"derivedFrom":[subQ2,subQ0]});Q4=makeQuery(id+"F16.boolean.opBoolean","SPLIT",EDGE,{"disambiguationData":[TD([makeQuery(id+"F14.opExtrude","CAP_FACE",FACE,{"disambiguationData":[OSD([subQ2,subQ0,subQ1])],"isStart":false})])],"derivedFrom":makeQuery(id+"FyxM6r6C1p8SssR_1.1.F14.opExtrude","SWEPT_EDGE",EDGE,{"disambiguationData":[OSD([subQ2,subQ0]),TDD([subQ3])]})});}
            var Q5;
            {var subQ0=sQuery(id+"F13.wireOp",EDGE,"E55");var subQ1=makeQuery(id+"FyxM6r6C1p8SssR_1.1.F14.opExtrude","SWEPT_FACE",FACE,{"disambiguationData":[OSD([subQ0])]});var subQ2=sQuery(id+"F13.wireOp",EDGE,"E56.MirrorC");var subQ3=sQuery(id+"F13.wireOp",EDGE,"E54");var subQ4=makeQuery(id+"F14.opExtrude","SWEPT_FACE",FACE,{"disambiguationData":[OSD([subQ0])]});Q5=makeQuery(id+"F16.boolean.opBoolean","SPLIT",EDGE,{"disambiguationData":[TD([makeQuery(id+"F14.opExtrude","CAP_FACE",FACE,{"disambiguationData":[OSD([subQ3,subQ0,subQ2])],"isStart":false})])],"derivedFrom":makeQuery(id+"FyxM6r6C1p8SssR_1.1.F14.boolean.opBoolean","INTERSECT",EDGE,{"disambiguationData":[OD(0.0)],"derivedFrom":[subQ4,subQ1]})});}
            var Q6;
            {var subQ0=sQuery(id+"F13.wireOp",EDGE,"E56.MirrorC");Q6=makeQuery(id+"FyxM6r6C1p8SssR_1.1.F14.boolean.opBoolean","INTERSECT",EDGE,{"disambiguationData":[OD(2.0)],"derivedFrom":[makeQuery(id+"F14.boolean.opBoolean","SPLIT",FACE,{"disambiguationData":[TD([makeQuery(id+"F2.opRevolve","SWEPT_FACE",FACE,{"disambiguationData":[OSD([sQuery(id+"F1.wireOp",EDGE,"E16.0")])]})])],"derivedFrom":makeQuery(id+"F14.opExtrude","SWEPT_FACE",FACE,{"disambiguationData":[OSD([subQ0])]})}),makeQuery(id+"FyxM6r6C1p8SssR_1.1.F14.opExtrude","SWEPT_FACE",FACE,{"disambiguationData":[OSD([subQ0])]})]});}
            var Q7;
            {var subQ0=sQuery(id+"F13.wireOp",EDGE,"E56.MirrorC");var subQ1=sQuery(id+"F13.wireOp",EDGE,"E55");var subQ2=sQuery(id+"F13.wireOp",EDGE,"E54");var subQ3=makeQuery(id+"F13.imprint","INTERSECT",VERTEX,{"disambiguationData":[OD(1.0)],"derivedFrom":[subQ2,subQ0]});Q7=makeQuery(id+"F16.boolean.opBoolean","SPLIT",EDGE,{"disambiguationData":[TD([makeQuery(id+"F14.opExtrude","CAP_FACE",FACE,{"disambiguationData":[OSD([subQ2,subQ1,subQ0])],"isStart":true})])],"derivedFrom":makeQuery(id+"FyxM6r6C1p8SssR_1.1.F14.opExtrude","SWEPT_EDGE",EDGE,{"disambiguationData":[OSD([subQ2,subQ0]),TDD([subQ3])]})});}
            var Q8;
            {var subQ0=sQuery(id+"F13.wireOp",EDGE,"E55");var subQ1=sQuery(id+"F13.wireOp",EDGE,"E54");var subQ2=makeQuery(id+"F13.imprint","INTERSECT",VERTEX,{"disambiguationData":[OD(1.0)],"derivedFrom":[subQ1,subQ0]});var subQ3=sQuery(id+"F13.wireOp",EDGE,"E56.MirrorC");Q8=makeQuery(id+"F16.boolean.opBoolean","SPLIT",EDGE,{"disambiguationData":[TD([makeQuery(id+"F14.opExtrude","CAP_FACE",FACE,{"disambiguationData":[OSD([subQ1,subQ0,subQ3])],"isStart":true})])],"derivedFrom":makeQuery(id+"FyxM6r6C1p8SssR_1.1.F14.opExtrude","SWEPT_EDGE",EDGE,{"disambiguationData":[OSD([subQ1,subQ0]),TDD([subQ2])]})});}
            var Q9;
            {var subQ0=sQuery(id+"F13.wireOp",EDGE,"E55");var subQ1=makeQuery(id+"FyxM6r6C1p8SssR_1.1.F14.opExtrude","SWEPT_FACE",FACE,{"disambiguationData":[OSD([subQ0])]});var subQ2=sQuery(id+"F13.wireOp",EDGE,"E56.MirrorC");var subQ3=sQuery(id+"F13.wireOp",EDGE,"E54");var subQ4=makeQuery(id+"F14.opExtrude","SWEPT_FACE",FACE,{"disambiguationData":[OSD([subQ0])]});Q9=makeQuery(id+"F16.boolean.opBoolean","SPLIT",EDGE,{"disambiguationData":[TD([makeQuery(id+"F14.opExtrude","CAP_FACE",FACE,{"disambiguationData":[OSD([subQ3,subQ0,subQ2])],"isStart":true})])],"derivedFrom":makeQuery(id+"FyxM6r6C1p8SssR_1.1.F14.boolean.opBoolean","INTERSECT",EDGE,{"disambiguationData":[OD(0.0)],"derivedFrom":[subQ4,subQ1]})});}
            var Q10;
            {var subQ0=sQuery(id+"F13.wireOp",EDGE,"E56.MirrorC");var subQ1=sQuery(id+"F13.wireOp",EDGE,"E55");var subQ2=sQuery(id+"F13.wireOp",EDGE,"E54");var subQ3=makeQuery(id+"F13.imprint","INTERSECT",VERTEX,{"disambiguationData":[OD(1.0)],"derivedFrom":[subQ2,subQ1]});Q10=makeQuery(id+"F16.boolean.opBoolean","SPLIT",EDGE,{"disambiguationData":[TD([makeQuery(id+"F14.opExtrude","CAP_FACE",FACE,{"disambiguationData":[OSD([subQ2,subQ1,subQ0])],"isStart":true})])],"derivedFrom":makeQuery(id+"F14.opExtrude","SWEPT_EDGE",EDGE,{"disambiguationData":[OSD([subQ2,subQ1]),TDD([subQ3])]})});}
            var Q11;
            {var subQ0=sQuery(id+"F13.wireOp",EDGE,"E56.MirrorC");var subQ1=sQuery(id+"F13.wireOp",EDGE,"E55");var subQ2=sQuery(id+"F13.wireOp",EDGE,"E54");var subQ3=makeQuery(id+"F13.imprint","INTERSECT",VERTEX,{"disambiguationData":[OD(1.0)],"derivedFrom":[subQ2,subQ0]});Q11=makeQuery(id+"F16.boolean.opBoolean","SPLIT",EDGE,{"disambiguationData":[TD([makeQuery(id+"F14.opExtrude","CAP_FACE",FACE,{"disambiguationData":[OSD([subQ2,subQ1,subQ0])],"isStart":true})])],"derivedFrom":makeQuery(id+"F14.opExtrude","SWEPT_EDGE",EDGE,{"disambiguationData":[OSD([subQ2,subQ0]),TDD([subQ3])]})});}
            fillet(context, id + "F26", {"entities" : qUnion([Q0, Q1, Q2, Q3, Q4, Q5, Q6, Q7, Q8, Q9, Q10, Q11]), "radius" : 0.3 * mm, "tangentPropagation" : true, "allowEdgeOverflow" : false});
        }
        {
            var Q0;
            {var subQ0=sQuery(id+"F13.wireOp",EDGE,"E56.MirrorC");var subQ1=sQuery(id+"F13.wireOp",EDGE,"E55");var subQ2=sQuery(id+"F13.wireOp",EDGE,"E54");Q0=makeQuery(id+"F23.boolean.opBoolean","INTERSECT",EDGE,{"derivedFrom":[makeQuery(id+"F20.boolean.opBoolean","MERGE",FACE,{"derivedFrom":[makeQuery(id+"FyxM6r6C1p8SssR_1.1.F14.boolean.opBoolean","MERGE",FACE,{"derivedFrom":[makeQuery(id+"F14.opExtrude","CAP_FACE",FACE,{"disambiguationData":[OSD([subQ2,subQ1,subQ0])],"isStart":true}),makeQuery(id+"FyxM6r6C1p8SssR_1.1.F14.opExtrude","CAP_FACE",FACE,{"disambiguationData":[OSD([subQ2,subQ1,subQ0])],"isStart":true})]}),makeQuery(id+"F20.opExtrude","CAP_FACE",FACE,{"disambiguationData":[OSD([sQuery(id+"F19.wireOp",EDGE,"E71.0"),sQuery(id+"F19.wireOp",EDGE,"E71.1"),sQuery(id+"F19.wireOp",EDGE,"E71.2"),sQuery(id+"F19.wireOp",EDGE,"E71.3")])],"isStart":false}),makeQuery(id+"F20.opExtrude","CAP_FACE",FACE,{"disambiguationData":[OSD([sQuery(id+"F19.wireOp",EDGE,"E71.4"),sQuery(id+"F19.wireOp",EDGE,"E71.5"),sQuery(id+"F19.wireOp",EDGE,"E71.6"),sQuery(id+"F19.wireOp",EDGE,"E71.7")])],"isStart":false})]}),makeQuery(id+"F23.opRevolve","SWEPT_FACE",FACE,{"disambiguationData":[OSD([sQuery(id+"F22.wireOp",EDGE,"E80.trimOffspring")])]})]});}
            fillet(context, id + "F27", {"entities" : qUnion([Q0]), "radius" : 1 * mm, "tangentPropagation" : true, "allowEdgeOverflow" : false});
        }
        {
            var Q0;
            Q0=makeQuery(id+"F23.boolean.opBoolean","COPY",EDGE,{"derivedFrom":makeQuery(id+"F23.opRevolve","SWEPT_EDGE",EDGE,{"disambiguationData":[OSD([sQuery(id+"F22.wireOp",EDGE,"E76.0"),sQuery(id+"F22.wireOp",EDGE,"E80.trimOffspring")])]})});
            var Q1;
            {var subQ0=sQuery(id+"F13.wireOp",EDGE,"E56.MirrorC");var subQ1=sQuery(id+"F13.wireOp",EDGE,"E55");var subQ2=sQuery(id+"F13.wireOp",EDGE,"E54");Q1=makeQuery(id+"F27.opFillet","BLEND_EDGE",EDGE,{"blendedFrom":[makeQuery(id+"F23.boolean.opBoolean","INTERSECT",EDGE,{"derivedFrom":[makeQuery(id+"F20.boolean.opBoolean","MERGE",FACE,{"derivedFrom":[makeQuery(id+"FyxM6r6C1p8SssR_1.1.F14.boolean.opBoolean","MERGE",FACE,{"derivedFrom":[makeQuery(id+"F14.opExtrude","CAP_FACE",FACE,{"disambiguationData":[OSD([subQ2,subQ1,subQ0])],"isStart":true}),makeQuery(id+"FyxM6r6C1p8SssR_1.1.F14.opExtrude","CAP_FACE",FACE,{"disambiguationData":[OSD([subQ2,subQ1,subQ0])],"isStart":true})]}),makeQuery(id+"F20.opExtrude","CAP_FACE",FACE,{"disambiguationData":[OSD([sQuery(id+"F19.wireOp",EDGE,"E71.0"),sQuery(id+"F19.wireOp",EDGE,"E71.1"),sQuery(id+"F19.wireOp",EDGE,"E71.2"),sQuery(id+"F19.wireOp",EDGE,"E71.3")])],"isStart":false}),makeQuery(id+"F20.opExtrude","CAP_FACE",FACE,{"disambiguationData":[OSD([sQuery(id+"F19.wireOp",EDGE,"E71.4"),sQuery(id+"F19.wireOp",EDGE,"E71.5"),sQuery(id+"F19.wireOp",EDGE,"E71.6"),sQuery(id+"F19.wireOp",EDGE,"E71.7")])],"isStart":false})]}),makeQuery(id+"F23.opRevolve","SWEPT_FACE",FACE,{"disambiguationData":[OSD([sQuery(id+"F22.wireOp",EDGE,"E80.trimOffspring")])]})]}),makeQuery(id+"F23.boolean.opBoolean","COPY",FACE,{"derivedFrom":makeQuery(id+"F23.opRevolve","SWEPT_FACE",FACE,{"disambiguationData":[OSD([sQuery(id+"F22.wireOp",EDGE,"E76.0")])]})})],"blendedInto":[makeQuery(id+"F23.boolean.opBoolean","COPY",FACE,{"derivedFrom":makeQuery(id+"F23.opRevolve","SWEPT_FACE",FACE,{"disambiguationData":[OSD([sQuery(id+"F22.wireOp",EDGE,"E76.0")])]})})]});}
            fillet(context, id + "F28", {"entities" : qUnion([Q0, Q1]), "radius" : 1 * mm, "tangentPropagation" : true, "allowEdgeOverflow" : false});
        }
        {
            var Q0;
            Q0=makeQuery(id+"F8.boolean.opBoolean","INTERSECT",EDGE,{"disambiguationData":[OD(0.0)],"derivedFrom":[makeQuery(id+"F7.opRevolve","SWEPT_FACE",FACE,{"disambiguationData":[OSD([sQuery(id+"F6.wireOp",EDGE,"E42")])]}),makeQuery(id+"F8.opExtrude","SWEPT_FACE",FACE,{"disambiguationData":[OSD([sQuery(id+"F5.wireOp",EDGE,"E38")])]})]});
            var Q1;
            Q1=makeQuery(id+"F8.boolean.opBoolean","INTERSECT",EDGE,{"disambiguationData":[OD(1.0)],"derivedFrom":[makeQuery(id+"F7.opRevolve","SWEPT_FACE",FACE,{"disambiguationData":[OSD([sQuery(id+"F6.wireOp",EDGE,"E42")])]}),makeQuery(id+"F8.opExtrude","SWEPT_FACE",FACE,{"disambiguationData":[OSD([sQuery(id+"F5.wireOp",EDGE,"E38")])]})]});
            var Q2;
            Q2=makeQuery(id+"F8.boolean.opBoolean","INTERSECT",EDGE,{"disambiguationData":[OD(1.0)],"derivedFrom":[makeQuery(id+"F4.boolean.opBoolean","COPY",FACE,{"derivedFrom":makeQuery(id+"F4.opRevolve","SWEPT_FACE",FACE,{"disambiguationData":[OSD([sQuery(id+"F3.wireOp",EDGE,"E31.0")])]})}),makeQuery(id+"F8.opExtrude","SWEPT_FACE",FACE,{"disambiguationData":[OSD([sQuery(id+"F5.wireOp",EDGE,"E38")])]})]});
            var Q3;
            Q3=makeQuery(id+"F8.boolean.opBoolean","INTERSECT",EDGE,{"disambiguationData":[OD(0.0)],"derivedFrom":[makeQuery(id+"F4.boolean.opBoolean","COPY",FACE,{"derivedFrom":makeQuery(id+"F4.opRevolve","SWEPT_FACE",FACE,{"disambiguationData":[OSD([sQuery(id+"F3.wireOp",EDGE,"E31.0")])]})}),makeQuery(id+"F8.opExtrude","SWEPT_FACE",FACE,{"disambiguationData":[OSD([sQuery(id+"F5.wireOp",EDGE,"E38")])]})]});
            fillet(context, id + "F29", {"entities" : qUnion([Q0, Q1, Q2, Q3]), "radius" : 0.3 * mm, "tangentPropagation" : true, "allowEdgeOverflow" : false});
        }
        {
            var Q0;
            Q0=makeQuery(id+"F29.opFillet","BLEND_EDGE",EDGE,{"blendedFrom":[makeQuery(id+"F8.boolean.opBoolean","INTERSECT",EDGE,{"disambiguationData":[OD(0.0)],"derivedFrom":[makeQuery(id+"F7.opRevolve","SWEPT_FACE",FACE,{"disambiguationData":[OSD([sQuery(id+"F6.wireOp",EDGE,"E42")])]}),makeQuery(id+"F8.opExtrude","SWEPT_FACE",FACE,{"disambiguationData":[OSD([sQuery(id+"F5.wireOp",EDGE,"E38")])]})]}),makeQuery(id+"F8.boolean.opBoolean","SPLIT",FACE,{"disambiguationData":[OD(0.0)],"derivedFrom":makeQuery(id+"F2.opRevolve","SWEPT_FACE",FACE,{"disambiguationData":[OSD([sQuery(id+"F1.wireOp",EDGE,"E18.0")])]})})],"blendedInto":[makeQuery(id+"F8.boolean.opBoolean","SPLIT",FACE,{"disambiguationData":[OD(0.0)],"derivedFrom":makeQuery(id+"F2.opRevolve","SWEPT_FACE",FACE,{"disambiguationData":[OSD([sQuery(id+"F1.wireOp",EDGE,"E18.0")])]})})]});
            var Q1;
            Q1=makeQuery(id+"F8.boolean.opBoolean","SPLIT",EDGE,{"disambiguationData":[OD(0.0)],"derivedFrom":makeQuery(id+"F4.boolean.opBoolean","INTERSECT",EDGE,{"derivedFrom":[makeQuery(id+"F2.opRevolve","SWEPT_FACE",FACE,{"disambiguationData":[OSD([sQuery(id+"F1.wireOp",EDGE,"E18.0")])]}),makeQuery(id+"F4.opRevolve","SWEPT_FACE",FACE,{"disambiguationData":[OSD([sQuery(id+"F3.wireOp",EDGE,"E31.0")])]})]})});
            var Q2;
            Q2=makeQuery(id+"F8.boolean.opBoolean","SPLIT",EDGE,{"disambiguationData":[OD(1.0)],"derivedFrom":makeQuery(id+"F4.boolean.opBoolean","INTERSECT",EDGE,{"derivedFrom":[makeQuery(id+"F2.opRevolve","SWEPT_FACE",FACE,{"disambiguationData":[OSD([sQuery(id+"F1.wireOp",EDGE,"E18.0")])]}),makeQuery(id+"F4.opRevolve","SWEPT_FACE",FACE,{"disambiguationData":[OSD([sQuery(id+"F3.wireOp",EDGE,"E31.0")])]})]})});
            var Q3;
            Q3=makeQuery(id+"F8.boolean.opBoolean","SPLIT",EDGE,{"disambiguationData":[OD(1.0)],"derivedFrom":makeQuery(id+"F7.boolean.opBoolean","MERGE",EDGE,{"derivedFrom":[makeQuery(id+"F2.opRevolve","SWEPT_EDGE",EDGE,{"disambiguationData":[OSD([sQuery(id+"F1.wireOp",EDGE,"E17.0"),sQuery(id+"F1.wireOp",EDGE,"E18.0")])]}),makeQuery(id+"F7.opRevolve","SWEPT_EDGE",EDGE,{"disambiguationData":[OSD([sQuery(id+"F6.wireOp",EDGE,"E40"),sQuery(id+"F6.wireOp",EDGE,"E42")])]})]})});
            fillet(context, id + "F30", {"entities" : qUnion([Q0, Q1, Q2, Q3]), "radius" : 0.2 * mm, "tangentPropagation" : true, "allowEdgeOverflow" : false});
        }
    });
